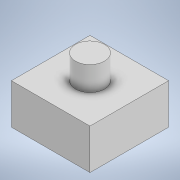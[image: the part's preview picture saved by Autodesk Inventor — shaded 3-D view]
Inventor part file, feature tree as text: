
AUTODESK INVENTOR PART (.ipt)
format: ipt  version: 2022 (Build 260153000, 153)  size: 99,840 bytes
history: native  units: in
note: dims shown in document units (in); Inventor stores cm internally (conversion verified against a paired STEP export)
features: extrude x2, sketch x2, projected_geometry x1
ambient origin geometry x8: Origin, YZ Plane, XZ Plane, XY Plane, X Axis, Y Axis, Z Axis, Center Point
bodies: Solid1 (feature_tree)
feature tree (5):
  extrude  "Extrusion1"  Depth=0.3839in
  extrude  "Extrusion2"  Depth=0.1181in
  sketch  "Sketch1"  dims[d0=0.3839in d1=0.3839in]
  sketch  "Sketch2"  dims[d2=0.1969in d3=0.0in d4=0.1417in d5=0.1181in d6=0.0in]
  projected_geometry  "Projected Loop1"
